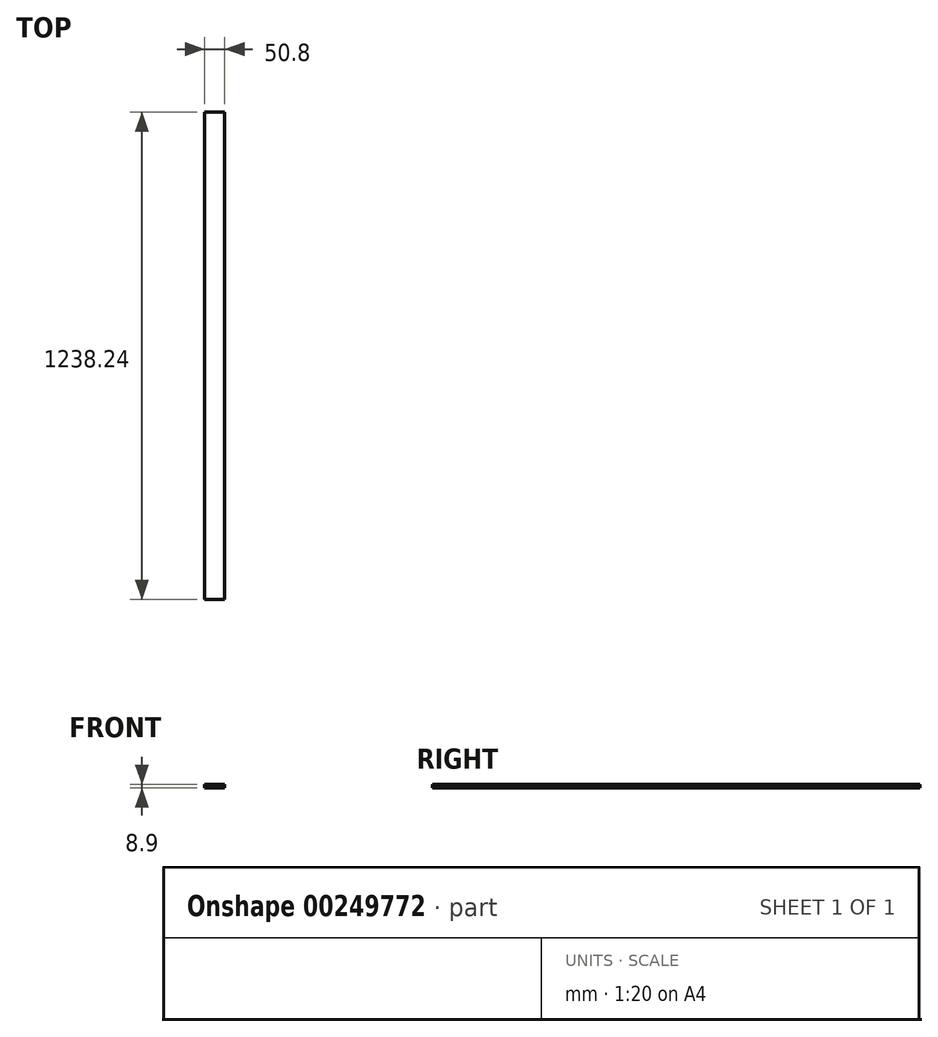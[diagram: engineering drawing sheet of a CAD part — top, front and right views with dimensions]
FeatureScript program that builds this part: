
annotation { "Feature Type Name" : "Feature", "Feature Type Description" : "" }
export const myFeature = defineFeature(function(context is Context, id is Id, definition is map)
    precondition{}
    {
        {
            var Q0;
            Q0=qCreatedBy(makeId("Front.planeOp"),FACE);
            var sketch = newSketch(context, id + "F0", { "sketchPlane" : qUnion([Q0])});
            skLineSegment(sketch, "E0.bottom", {"start": v(25.4, -4.44) * mm, "end": v(-25.4, -4.45) * mm});
            skLineSegment(sketch, "E0.top", {"start": v(25.4, 4.45) * mm, "end": v(-25.4, 4.44) * mm});
            skLineSegment(sketch, "E0.left", {"start": v(25.4, -4.44) * mm, "end": v(25.4, 4.45) * mm});
            skLineSegment(sketch, "E0.right", {"start": v(-25.4, -4.45) * mm, "end": v(-25.4, 4.44) * mm});
            skPoint(sketch, "E0.middle", {"position": v(0, 0) * mm});
            skSolve(sketch);
        }
        {
            var Q0;
            Q0 = qSketchRegion(id + "F0", true);
            extrude(context, id + "F1", {"entities" : qUnion([Q0]), "depth" : 1238.25 * mm, "symmetric" : true});
        }
    });
